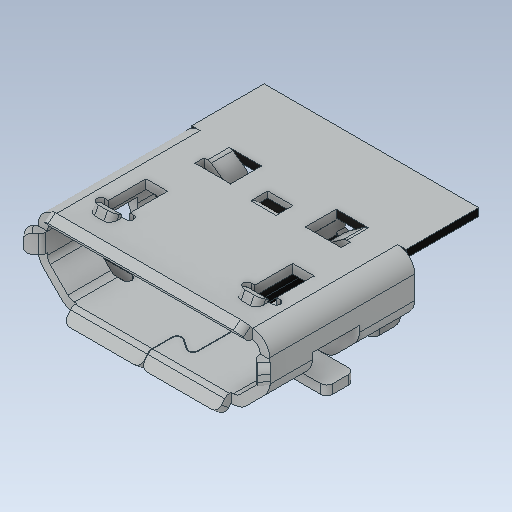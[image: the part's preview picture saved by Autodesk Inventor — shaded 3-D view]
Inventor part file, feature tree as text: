
AUTODESK INVENTOR PART (.ipt)
format: ipt  version: 2020.1 (Build 241239000, 239)  size: 542,208 bytes
history: mixed  units: mm
features: extrude x2, sketch x2, fillet x1, imported_body x1
ambient origin geometry x8: Origin, YZ Plane, XZ Plane, XY Plane, X Axis, Y Axis, Z Axis, Center Point
bodies: Solid1 (imported_parasolid)
feature tree (6):
  extrude  "Extrusion1"  Depth=4.7mm
  extrude  "Extrusion2"  Depth=0.5mm
  sketch  "Sketch1"  dims[d0=2.35mm d1=4.7mm]
  sketch  "Sketch2"  dims[d2=0.25mm d3=0.0mm d4=0.5mm d5=50.0mm d7=1.3mm d8=10.0mm d10=10.0mm d13=0.1mm d14=0.0mm]
  fillet  "Fillet13"  Radius=1.3mm
  imported_body  NMx_Import_Brep_tag  [imported B-rep: ~345 faces, bbox_mm=[7.98, 2.783674, 7.48]]
